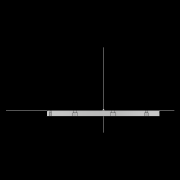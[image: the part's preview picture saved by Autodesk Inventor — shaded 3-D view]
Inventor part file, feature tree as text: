
AUTODESK INVENTOR PART (.ipt)
format: ipt  version: 2022.2 (Build 262287010, 287A)  size: 724,992 bytes
history: native  units: mm
features: extrude x19, sketch x18, pattern_circular x15, other x14, revolve x7, hole x7, move_body x4, fillet x2, draft x2
ambient origin geometry x8: Origin, YZ Plane, XZ Plane, XY Plane, X Axis, Y Axis, Z Axis, Center Point
bodies: Solid1 (feature_tree), Solid2 (feature_tree), Solid3 (feature_tree), Solid4 (feature_tree), Solid5 (feature_tree)
feature tree (88):
  sketch  "Sketch7"  dims[d21=0.5mm]
  other  "Roller1"
  other  "Roller2"
  sketch  "Sketch22"  dims[d39=0.05mm]
  sketch  "Sketch2"  dims[d17=0.05mm]
  sketch  "Sketch23"  dims[d41=0.05mm]
  other  "RevRoller1"
  fillet  "Fillet1"  Radius=0.05mm
  pattern_circular  "Circular Pattern13"  Count=6  [1 undecoded]
  move_body  "Move Body7"
  revolve  "Revolution13"  Angle=30.0deg
  fillet  "Fillet3"  [1 undecoded]
  pattern_circular  "Circular Pattern14"  [2 undecoded]
  move_body  "Move Body6"
  revolve  "Revolution14"  [1 undecoded]
  other  "OuterRim_Top2"
  other  "OuterRim_Bottom2"
  extrude  "Extrusion9"  TaperAngle=90.0deg  [1 undecoded]
  sketch  "Sketch24"  dims[d42=0.5mm]
  extrude  "Extrusion10"  Depth=1.5mm
  extrude  "Extrusion11"  Depth=1.5mm
  pattern_circular  "Circular Pattern15"  [2 undecoded]
  sketch  "Sketch25"  dims[d43=0.5mm]
  extrude  "Extrusion12"  Depth=1.5mm
  extrude  "Extrusion14"  Depth=1.5mm
  extrude  "Extrusion15"  Depth=1.5mm
  pattern_circular  "Circular Pattern16"  [2 undecoded]
  extrude  "Extrusion16"  Depth=1.5mm
  extrude  "Extrusion17"  Depth=1.5mm
  hole  "Hole9"  [1 undecoded]
  pattern_circular  "Circular Pattern17"  [2 undecoded]
  sketch  "Sketch27"  dims[d45=0.5mm]
  hole  "Hole10"  [1 undecoded]
  hole  "Hole11"  [1 undecoded]
  pattern_circular  "Circular Pattern18"  [2 undecoded]
  extrude  "Extrusion18"  Depth=1.5mm
  extrude  "Extrusion19"  Depth=1.5mm
  pattern_circular  "Circular Pattern19"  [2 undecoded]
  sketch  "Sketch28"  dims[d46=0.5mm d47=0.5mm d48=2.0mm d50=90.0deg d56=14.029612mm d57=4.025mm d90=16.473921mm d107=0.05mm d108=0.05mm d109=0.05mm d110=0.05mm d112=0.5mm d113=0.5mm d114=0.5mm d115=14.644822mm d116=14.607374mm d117=1.0mm d118=0.05mm d119=0.05mm d120=0.05mm d121=0.05mm d122=0.5mm d123=0.5mm d124=14.644822mm d125=14.607374mm d126=1.0mm d127=90.0deg d128=30.0deg d129=90.0deg d167=8.972256mm d173=10.814812mm d201=53.5mm d202=90.0deg d203=90.0deg d204=90.0deg d218=53.5mm d226=5.4mm d232=0.0mm d233=3600.0mm d234=10.502mm d235=0.0mm d243=1.902mm d244=0.0mm d246=2.75mm d247=5.251mm d248=0.0mm d249=3.0mm d250=0.0mm d251=90.0mm d252=360.0deg d254=2.75mm d255=3.0mm d256=5.251mm d257=0.0mm d258=3.0mm d259=0.0mm d260=90.0mm d261=360.0deg d277=76.5mm d281=73.5mm d282=24.65mm d283=6.0mm d284=4.0mm d285=2.0mm d286=90.0deg d287=5.251mm d288=0.0mm d289=60.0mm d290=360.0deg d292=0.436332mm d293=60.0mm d294=90.0mm d295=3.0mm d296=6.0mm d297=5.5mm d298=3.0mm d299=90.0deg d300=5.251mm d301=0.0mm d302=60.0mm d303=360.0deg d305=30.0deg d306=73.5mm d307=24.65mm d308=6.0mm d309=5.5mm d310=3.0mm d311=90.0deg d312=5.251mm d313=0.0mm d314=60.0mm d315=360.0deg d317=90.0mm d318=60.0mm d319=30.0deg d320=5.4mm d321=5.4mm d322=3.0mm d323=6.0mm d324=5.5mm d325=3.0mm d326=90.0deg d327=5.251mm d328=0.0mm d329=2.4mm d330=0.0mm d331=60.0mm d332=360.0deg d343=17.307186mm d344=17.309884mm d345=0.025mm d346=0.025mm d347=0.1mm d348=0.1mm d349=17.309884mm d350=17.307186mm d351=0.025mm d352=0.025mm d354=0.1mm d355=17.307186mm d356=17.309884mm d357=1.0mm d358=90.0deg d359=0.5mm d360=60.0mm d361=360.0deg d363=30.0deg d367=8.1mm d369=4.014775mm d370=0.1mm d371=1.0mm d372=30.0deg d373=90.0deg d374=0.5mm d375=60.0mm d376=360.0deg d378=90.0deg d379=0.1mm d380=0.1mm d381=0.1mm d382=0.1mm d383=0.1mm d384=10.502mm d385=0.0mm d386=0.0mm d391=1.0mm d392=53.5mm d393=1.5mm d394=1.5mm d395=1.5mm d396=1.5mm d397=90.0deg d398=90.0deg d399=90.0deg d400=53.5mm d401=10.502mm d402=0.0mm d403=2.75mm d404=1.5mm d405=10.502mm d406=0.0mm d407=3.0mm d408=0.0mm d409=90.0mm d410=360.0deg d412=5.4mm d413=5.251mm d414=0.0mm d417=5.4mm d418=2.4mm d419=0.0mm d420=2.4mm d421=0.0mm d422=90.0mm d423=360.0deg d425=60.0mm d426=90.0mm d427=1.5mm d428=1.5mm d429=5.4mm d430=5.4mm d431=5.251mm d432=0.0mm d433=2.4mm d434=0.0mm d435=30.0deg d436=73.5mm d437=24.65mm d438=6.0mm d439=4.0mm d440=2.0mm d441=90.0deg d442=5.251mm d443=0.0mm d444=60.0mm d445=360.0deg d447=3.0mm d448=6.0mm d449=5.5mm d450=3.0mm d451=90.0deg d452=5.251mm d453=0.0mm d454=24.65mm d455=6.0mm d456=5.5mm d457=3.0mm d458=90.0deg d459=5.251mm d460=0.0mm d461=60.0mm d462=360.0deg d464=5.251mm d465=0.0mm d466=3.0mm d467=0.0mm d468=90.0mm d469=360.0deg d472=1.5mm d474=5.251mm d475=0.0mm d481=3.0mm d482=0.0mm d483=90.0mm d484=360.0deg d486=0.436332mm d49=0.872665mm d51=0.872665mm d52=0.872665mm d236=0.5mm d237=0.872665mm d238=0.5mm d239=0.872665mm d291=0.0625mm d415=0.5mm d416=0.872665mm d471=0.5mm d473=0.5mm]
  extrude  "Extrusion20"  Depth=1.5mm
  extrude  "Extrusion22"  Depth=1.5mm
  pattern_circular  "Circular Pattern21"  [2 undecoded]
  draft  "FaceDraft2"
  other  "InnerRim"
  other  "OuterRim_Top"
  other  "OuterRim_Bottom"
  extrude  "Extrusion2"  Depth=1.5mm
  sketch  "Sketch13"  dims[d24=0.5mm]
  extrude  "Extrusion3"  Depth=1.5mm
  sketch  "Sketch15"  dims[d29=360.0deg d30=60.0mm]
  extrude  "Extrusion4"  TaperAngle=90.0deg  [1 undecoded]
  extrude  "Extrusion5"  TaperAngle=30.0deg  [1 undecoded]
  pattern_circular  "Circular Pattern6"  Angle=90.0deg  [1 undecoded]
  sketch  "Sketch16"  dims[d31=360.0deg d35=30.0deg d36=90.0deg]
  extrude  "Extrusion6"  Depth=1.5mm
  extrude  "Extrusion7"  Depth=1.5mm
  pattern_circular  "Circular Pattern7"  [2 undecoded]
  hole  "Hole5"  [1 undecoded]
  pattern_circular  "Circular Pattern9"  Angle=90.0deg  [1 undecoded]
  draft  "FaceDraft1"
  hole  "Hole6"  [1 undecoded]
  pattern_circular  "Circular Pattern10"  [2 undecoded]
  hole  "Hole7"  [1 undecoded]
  pattern_circular  "Circular Pattern11"  Count=360  [1 undecoded]
  hole  "Hole8"  [1 undecoded]
  extrude  "Extrusion8"  TaperAngle=0.0deg  [1 undecoded]
  pattern_circular  "Circular Pattern12"  [2 undecoded]
  sketch  "Sketch8"  dims[d22=0.5mm]
  sketch  "Sketch9"  dims[d23=0.5mm]
  revolve  "Revolution4"  [1 undecoded]
  move_body  "Move Body4"
  revolve  "Revolution5"  [1 undecoded]
  sketch  "Sketch5"  dims[d19=0.5mm]
  sketch  "Sketch6"  dims[d20=0.5mm]
  revolve  "Revolution3"  [1 undecoded]
  sketch  "Sketch4"  dims[d18=0.05mm]
  revolve  "Revolution1"  [1 undecoded]
  pattern_circular  "Circular Pattern1"  [2 undecoded]
  move_body  "Move Body3"
  revolve  "Revolution2"  [1 undecoded]
  other  "2D Equation Curve1"
  sketch  "Sketch14"  dims[d28=2.0mm]
  other  "Work Axis1"
  other  "Work Axis2"
  other  "Work Axis3"
  other  "Work Axis4"
  other  "Work Axis5"
  sketch  "Sketch26"  dims[d44=0.5mm]
note: 44 required parameter values undecoded (feature->parameter linkage not recoverable at this tier; creation-order binding heuristic only, values carry confidence <= 0.55)